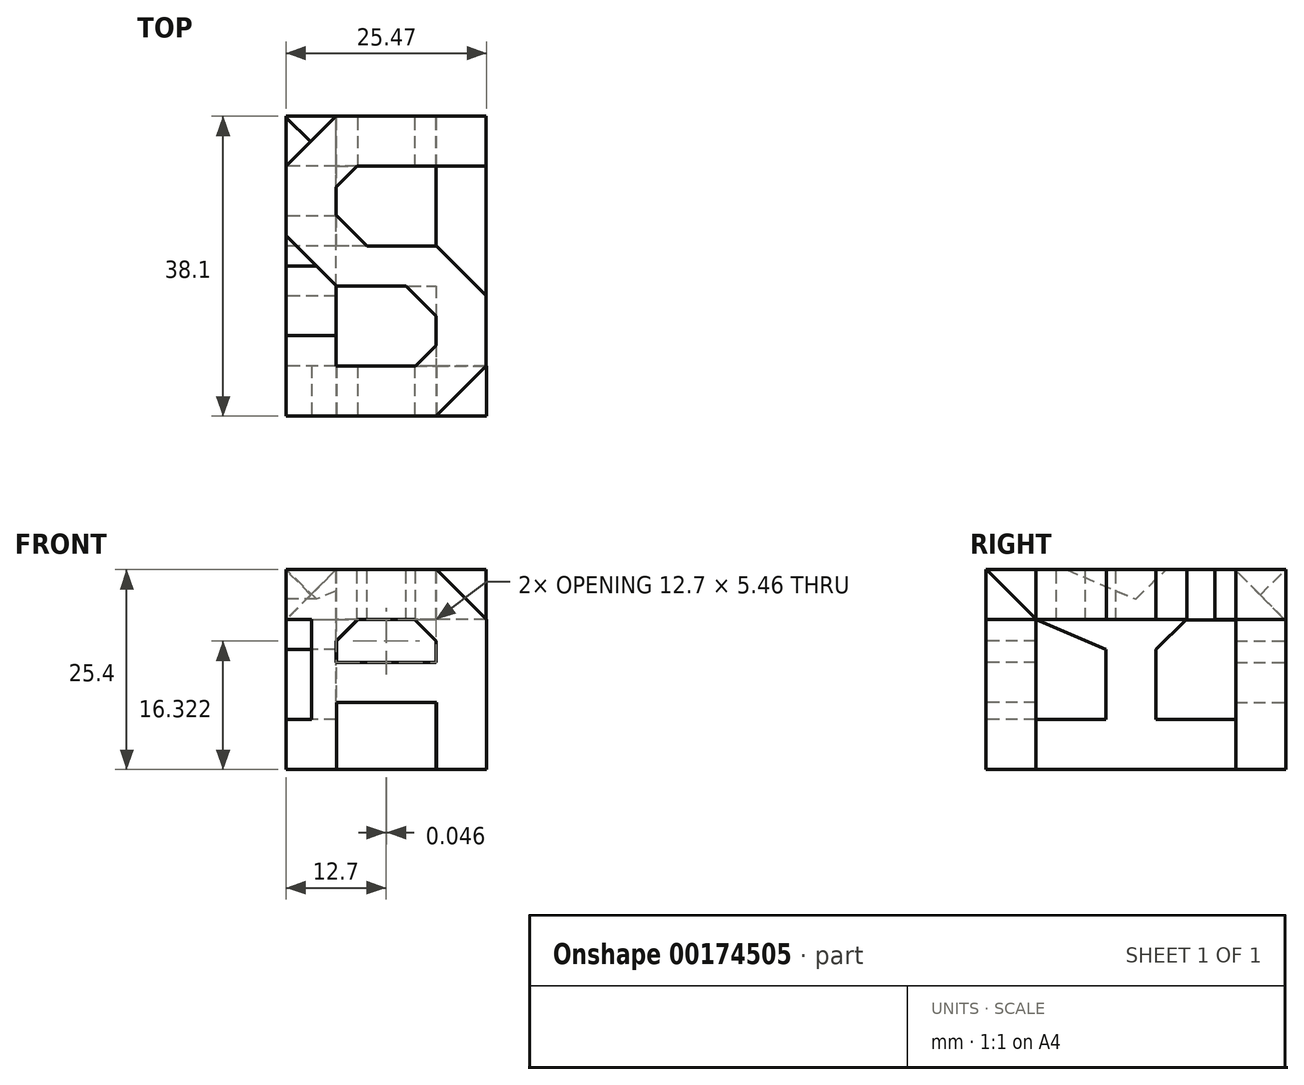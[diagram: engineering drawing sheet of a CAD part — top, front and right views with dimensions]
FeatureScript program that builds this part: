
annotation { "Feature Type Name" : "Feature", "Feature Type Description" : "" }
export const myFeature = defineFeature(function(context is Context, id is Id, definition is map)
    precondition{}
    {
        {
            var Q0;
            Q0=qCreatedBy(makeId("Top.planeOp"),FACE);
            var sketch = newSketch(context, id + "F0", { "sketchPlane" : qUnion([Q0])});
            skLineSegment(sketch, "E0", {"start": v(-12.7, 12.7) * mm, "end": v(-12.7, 0) * mm});
            skLineSegment(sketch, "E1", {"start": v(-12.7, 0) * mm, "end": v(-12.7, -12.7) * mm});
            skLineSegment(sketch, "E2", {"start": v(-12.7, -12.7) * mm, "end": v(-6.35, -12.7) * mm});
            skLineSegment(sketch, "E3", {"start": v(-6.35, -12.7) * mm, "end": v(-6.35, -2.54) * mm});
            skLineSegment(sketch, "E4", {"start": v(-6.35, -2.54) * mm, "end": v(0, -2.54) * mm});
            skLineSegment(sketch, "E5", {"start": v(0, -2.54) * mm, "end": v(6.35, -2.54) * mm});
            skLineSegment(sketch, "E6", {"start": v(6.35, -2.54) * mm, "end": v(6.35, -12.7) * mm});
            skLineSegment(sketch, "E7", {"start": v(6.35, -12.7) * mm, "end": v(12.7, -12.7) * mm});
            skLineSegment(sketch, "E8", {"start": v(12.7, -12.7) * mm, "end": v(12.7, 0) * mm});
            skLineSegment(sketch, "E9", {"start": v(12.7, 0) * mm, "end": v(12.7, 12.7) * mm});
            skLineSegment(sketch, "E10", {"start": v(12.7, 12.7) * mm, "end": v(6.35, 12.7) * mm});
            skLineSegment(sketch, "E11", {"start": v(6.35, 12.7) * mm, "end": v(6.35, 2.54) * mm});
            skLineSegment(sketch, "E12", {"start": v(6.35, 2.54) * mm, "end": v(0, 2.54) * mm});
            skLineSegment(sketch, "E13", {"start": v(0, 2.54) * mm, "end": v(-6.35, 2.54) * mm});
            skLineSegment(sketch, "E14", {"start": v(-6.35, 2.54) * mm, "end": v(-6.35, 12.7) * mm});
            skLineSegment(sketch, "E15", {"start": v(-6.35, 12.7) * mm, "end": v(-12.7, 12.7) * mm});
            skSolve(sketch);
        }
        {
            var Q0;
            Q0=makeQuery(id+"F0.imprint","IMPRINT",FACE,{"disambiguationData":[TD([[makeQuery(id+"F0.imprint","IMPRINT",EDGE,{"derivedFrom":sQuery(id+"F0.wireOp",EDGE,"E0")}),1.0]])]});
            extrude(context, id + "F1", {"entities" : qUnion([Q0]), "depth" : 1 / 101.6 * mm});
        }
        {
            var Q0;
            Q0=qCreatedBy(makeId("Front.planeOp"),FACE);
            cPlane(context, id + "F2", {"entities" : qUnion([Q0]), "cplaneType" : CPlaneType.OFFSET, "offset" : 19.05 * mm, "width" : 152.4 * mm, "height" : 152.4 * mm});
        }
        {
            var Q0;
            Q0=qCreatedBy(id+"F2.planeOp",FACE);
            var sketch = newSketch(context, id + "F3", { "sketchPlane" : qUnion([Q0])});
            skLineSegment(sketch, "E16", {"start": v(-12.63, 19.05) * mm, "end": v(-6.28, 25.4) * mm});
            skLineSegment(sketch, "E17", {"start": v(-6.28, 25.4) * mm, "end": v(6.42, 25.4) * mm});
            skLineSegment(sketch, "E18", {"start": v(6.42, 25.4) * mm, "end": v(12.77, 19.05) * mm});
            skLineSegment(sketch, "E19", {"start": v(12.77, 19.05) * mm, "end": v(12.77, 0) * mm});
            skLineSegment(sketch, "E20", {"start": v(12.77, 0) * mm, "end": v(6.42, 0) * mm});
            skLineSegment(sketch, "E21", {"start": v(6.42, 0) * mm, "end": v(6.42, 8.51) * mm});
            skLineSegment(sketch, "E22", {"start": v(6.42, 8.51) * mm, "end": v(-6.28, 8.51) * mm});
            skLineSegment(sketch, "E23", {"start": v(-6.28, 8.51) * mm, "end": v(-6.28, 0) * mm});
            skLineSegment(sketch, "E24", {"start": v(-6.28, 0) * mm, "end": v(-12.63, 0) * mm});
            skLineSegment(sketch, "E25", {"start": v(-6.35, 13.6) * mm, "end": v(6.35, 13.6) * mm});
            skLineSegment(sketch, "E26", {"start": v(6.35, 13.6) * mm, "end": v(6.35, 19.05) * mm});
            skLineSegment(sketch, "E27", {"start": v(-6.35, 19.05) * mm, "end": v(-6.35, 13.6) * mm});
            skLineSegment(sketch, "E28", {"start": v(6.42, 0) * mm, "end": v(6.42, 25.4) * mm});
            skLineSegment(sketch, "E29", {"start": v(0.07, 8.51) * mm, "end": v(0.07, 13.6) * mm});
            skLineSegment(sketch, "E30", {"start": v(-6.35, 16.32) * mm, "end": v(6.35, 16.32) * mm});
            skLineSegment(sketch, "E31", {"start": v(0, 15.24) * mm, "end": v(-6.35, 15.24) * mm});
            skLineSegment(sketch, "E32", {"start": v(-6.35, 16.32) * mm, "end": v(-3.62, 19.05) * mm});
            skLineSegment(sketch, "E33", {"start": v(-3.62, 19.05) * mm, "end": v(0, 19.05) * mm});
            skLineSegment(sketch, "E34", {"start": v(0, 19.05) * mm, "end": v(3.62, 19.05) * mm});
            skLineSegment(sketch, "E35", {"start": v(3.62, 19.05) * mm, "end": v(6.35, 16.32) * mm});
            skLineSegment(sketch, "E36", {"start": v(-12.63, 6.35) * mm, "end": v(-9.46, 6.35) * mm});
            skLineSegment(sketch, "E37", {"start": v(-9.46, 6.35) * mm, "end": v(-9.46, 19.05) * mm});
            skLineSegment(sketch, "E38", {"start": v(-9.46, 19.05) * mm, "end": v(-12.63, 19.05) * mm});
            skLineSegment(sketch, "E39", {"start": v(-12.63, 6.35) * mm, "end": v(-12.63, 0) * mm});
            skSolve(sketch);
        }
        {
            var Q0;
            Q0 = qSketchRegion(id + "F3", true);
            extrude(context, id + "F4", {"entities" : qUnion([Q0]), "operationType" : NewBodyOperationType.ADD, "oppositeDirection" : true, "depth" : 6.35 * mm});
        }
        {
            var Q0;
            Q0=qCreatedBy(makeId("Front.planeOp"),FACE);
            cPlane(context, id + "F5", {"entities" : qUnion([Q0]), "cplaneType" : CPlaneType.OFFSET, "offset" : 19.05 * mm, "oppositeDirection" : true, "width" : 152.4 * mm, "height" : 152.4 * mm});
        }
        {
            var Q0;
            Q0=qCreatedBy(id+"F5.planeOp",FACE);
            var sketch = newSketch(context, id + "F6", { "sketchPlane" : qUnion([Q0])});
            skLineSegment(sketch, "E40", {"start": v(12.7, 0) * mm, "end": v(12.7, 19.05) * mm});
            skLineSegment(sketch, "E41", {"start": v(12.7, 19.05) * mm, "end": v(6.38, 25.4) * mm});
            skLineSegment(sketch, "E42", {"start": v(6.38, 25.4) * mm, "end": v(-6.35, 25.4) * mm});
            skLineSegment(sketch, "E43", {"start": v(-6.35, 25.4) * mm, "end": v(-12.7, 19.05) * mm});
            skLineSegment(sketch, "E44", {"start": v(-12.7, 19.05) * mm, "end": v(-12.7, 0) * mm});
            skLineSegment(sketch, "E45", {"start": v(-12.7, 0) * mm, "end": v(-6.35, 0) * mm});
            skLineSegment(sketch, "E46", {"start": v(-6.35, 0) * mm, "end": v(-6.35, 8.51) * mm});
            skLineSegment(sketch, "E47", {"start": v(-6.35, 8.51) * mm, "end": v(6.35, 8.51) * mm});
            skLineSegment(sketch, "E48", {"start": v(6.35, 8.51) * mm, "end": v(6.35, 0) * mm});
            skLineSegment(sketch, "E49", {"start": v(6.35, 0) * mm, "end": v(12.7, 0) * mm});
            skLineSegment(sketch, "E50", {"start": v(6.4, 13.6) * mm, "end": v(6.4, 16.31) * mm});
            skLineSegment(sketch, "E51", {"start": v(6.4, 16.31) * mm, "end": v(3.68, 19.05) * mm});
            skLineSegment(sketch, "E52", {"start": v(3.68, 19.05) * mm, "end": v(-3.58, 19.05) * mm});
            skLineSegment(sketch, "E53", {"start": v(-3.58, 19.05) * mm, "end": v(-6.3, 16.31) * mm});
            skLineSegment(sketch, "E54", {"start": v(-6.3, 16.31) * mm, "end": v(-6.3, 13.6) * mm});
            skLineSegment(sketch, "E55", {"start": v(-6.3, 13.6) * mm, "end": v(6.4, 13.6) * mm});
            skSolve(sketch);
        }
        {
            var Q0;
            Q0=makeQuery(id+"F6.imprint","IMPRINT",FACE,{"disambiguationData":[TD([[makeQuery(id+"F6.imprint","IMPRINT",EDGE,{"derivedFrom":sQuery(id+"F6.wireOp",EDGE,"E40")}),1.0]])]});
            extrude(context, id + "F7", {"entities" : qUnion([Q0]), "operationType" : NewBodyOperationType.ADD, "depth" : 6.35 * mm});
        }
        {
            var Q0;
            Q0=qCreatedBy(makeId("Top.planeOp"),FACE);
            cPlane(context, id + "F8", {"entities" : qUnion([Q0]), "cplaneType" : CPlaneType.OFFSET, "offset" : 25.4 * mm, "width" : 152.4 * mm, "height" : 152.4 * mm});
        }
        {
            var Q0;
            Q0=qCreatedBy(id+"F8.planeOp",FACE);
            var sketch = newSketch(context, id + "F9", { "sketchPlane" : qUnion([Q0])});
            skLineSegment(sketch, "E56", {"start": v(12.7, 19.05) * mm, "end": v(-6.35, 19.05) * mm});
            skLineSegment(sketch, "E57", {"start": v(-6.35, 19.05) * mm, "end": v(-12.7, 12.7) * mm});
            skLineSegment(sketch, "E58", {"start": v(-12.7, 12.7) * mm, "end": v(-12.7, 3.87) * mm});
            skLineSegment(sketch, "E59", {"start": v(-12.7, 3.87) * mm, "end": v(-6.3, -2.54) * mm});
            skLineSegment(sketch, "E60", {"start": v(-6.3, -2.54) * mm, "end": v(2.53, -2.54) * mm});
            skLineSegment(sketch, "E61", {"start": v(2.53, -2.54) * mm, "end": v(6.35, -6.36) * mm});
            skLineSegment(sketch, "E62", {"start": v(6.35, -6.36) * mm, "end": v(6.35, -10.07) * mm});
            skLineSegment(sketch, "E63", {"start": v(6.35, -10.07) * mm, "end": v(3.72, -12.7) * mm});
            skLineSegment(sketch, "E64", {"start": v(3.72, -12.7) * mm, "end": v(-12.7, -12.7) * mm});
            skLineSegment(sketch, "E65", {"start": v(-12.7, -12.7) * mm, "end": v(-12.7, -19.05) * mm});
            skLineSegment(sketch, "E66", {"start": v(-12.7, -19.05) * mm, "end": v(6.35, -19.05) * mm});
            skLineSegment(sketch, "E67", {"start": v(6.35, -19.05) * mm, "end": v(12.7, -12.7) * mm});
            skLineSegment(sketch, "E68", {"start": v(12.7, -12.7) * mm, "end": v(12.7, -3.73) * mm});
            skLineSegment(sketch, "E69", {"start": v(12.7, -3.73) * mm, "end": v(6.43, 2.54) * mm});
            skLineSegment(sketch, "E70", {"start": v(-6.35, 10.07) * mm, "end": v(-3.72, 12.7) * mm});
            skLineSegment(sketch, "E71", {"start": v(-3.72, 12.7) * mm, "end": v(12.7, 12.7) * mm});
            skLineSegment(sketch, "E72", {"start": v(12.7, 12.7) * mm, "end": v(12.7, 19.05) * mm});
            skLineSegment(sketch, "E73", {"start": v(-6.35, 10.07) * mm, "end": v(-6.35, 6.5) * mm});
            skLineSegment(sketch, "E74", {"start": v(-6.35, 6.5) * mm, "end": v(-2.4, 2.54) * mm});
            skLineSegment(sketch, "E75", {"start": v(-2.4, 2.54) * mm, "end": v(6.43, 2.54) * mm});
            skSolve(sketch);
        }
        {
            var Q0;
            Q0 = qSketchRegion(id + "F9", true);
            extrude(context, id + "F10", {"entities" : qUnion([Q0]), "operationType" : NewBodyOperationType.ADD, "oppositeDirection" : true, "depth" : 6.35 * mm});
        }
        {
            var Q0;
            Q0=qCreatedBy(makeId("Right.planeOp"),FACE);
            cPlane(context, id + "F11", {"entities" : qUnion([Q0]), "cplaneType" : CPlaneType.OFFSET, "offset" : 12.7 * mm, "oppositeDirection" : true, "width" : 152.4 * mm, "height" : 152.4 * mm});
        }
        {
            var Q0;
            Q0=qCreatedBy(id+"F11.planeOp",FACE);
            var sketch = newSketch(context, id + "F12", { "sketchPlane" : qUnion([Q0])});
            skLineSegment(sketch, "E76", {"start": v(19.05, 0) * mm, "end": v(19.05, 18.9) * mm});
            skLineSegment(sketch, "E77", {"start": v(12.65, 25.37) * mm, "end": v(3.81, 25.37) * mm});
            skLineSegment(sketch, "E78", {"start": v(19.05, 0) * mm, "end": v(-19.05, 0) * mm});
            skLineSegment(sketch, "E79", {"start": v(-19.05, 0) * mm, "end": v(-19.05, 6.35) * mm});
            skLineSegment(sketch, "E80", {"start": v(-19.05, 6.35) * mm, "end": v(-3.81, 6.35) * mm});
            skLineSegment(sketch, "E81", {"start": v(-3.81, 6.35) * mm, "end": v(-3.81, 15.28) * mm});
            skLineSegment(sketch, "E82", {"start": v(-3.81, 15.28) * mm, "end": v(-12.7, 19.05) * mm});
            skLineSegment(sketch, "E83", {"start": v(-12.7, 19.05) * mm, "end": v(-19.04, 19.05) * mm});
            skLineSegment(sketch, "E84", {"start": v(-19.04, 19.05) * mm, "end": v(-19.04, 25.4) * mm});
            skLineSegment(sketch, "E85", {"start": v(-19.04, 25.4) * mm, "end": v(-8.8, 25.4) * mm});
            skLineSegment(sketch, "E86", {"start": v(-8.8, 25.4) * mm, "end": v(0, 21.67) * mm});
            skLineSegment(sketch, "E87", {"start": v(0, 21.67) * mm, "end": v(3.81, 25.37) * mm});
            skLineSegment(sketch, "E88", {"start": v(2.54, 6.35) * mm, "end": v(12.7, 6.35) * mm});
            skLineSegment(sketch, "E89", {"start": v(12.7, 6.35) * mm, "end": v(12.7, 19.02) * mm});
            skLineSegment(sketch, "E90", {"start": v(12.7, 19.02) * mm, "end": v(6.39, 19.02) * mm});
            skLineSegment(sketch, "E91", {"start": v(6.39, 19.02) * mm, "end": v(2.54, 15.28) * mm});
            skLineSegment(sketch, "E92", {"start": v(2.54, 15.28) * mm, "end": v(2.54, 6.35) * mm});
            skLineSegment(sketch, "E93", {"start": v(19.05, 18.9) * mm, "end": v(12.65, 25.37) * mm});
            skLineSegment(sketch, "E94", {"start": v(-8.8, 25.4) * mm, "end": v(-8.8, 19.52) * mm});
            skLineSegment(sketch, "E95", {"start": v(-12.7, 19.05) * mm, "end": v(-12.7, 23) * mm});
            skSolve(sketch);
        }
        {
            var Q0;
            Q0 = qSketchRegion(id + "F12", true);
            extrude(context, id + "F13", {"entities" : qUnion([Q0]), "operationType" : NewBodyOperationType.ADD, "depth" : 6.35 * mm});
        }
    });
